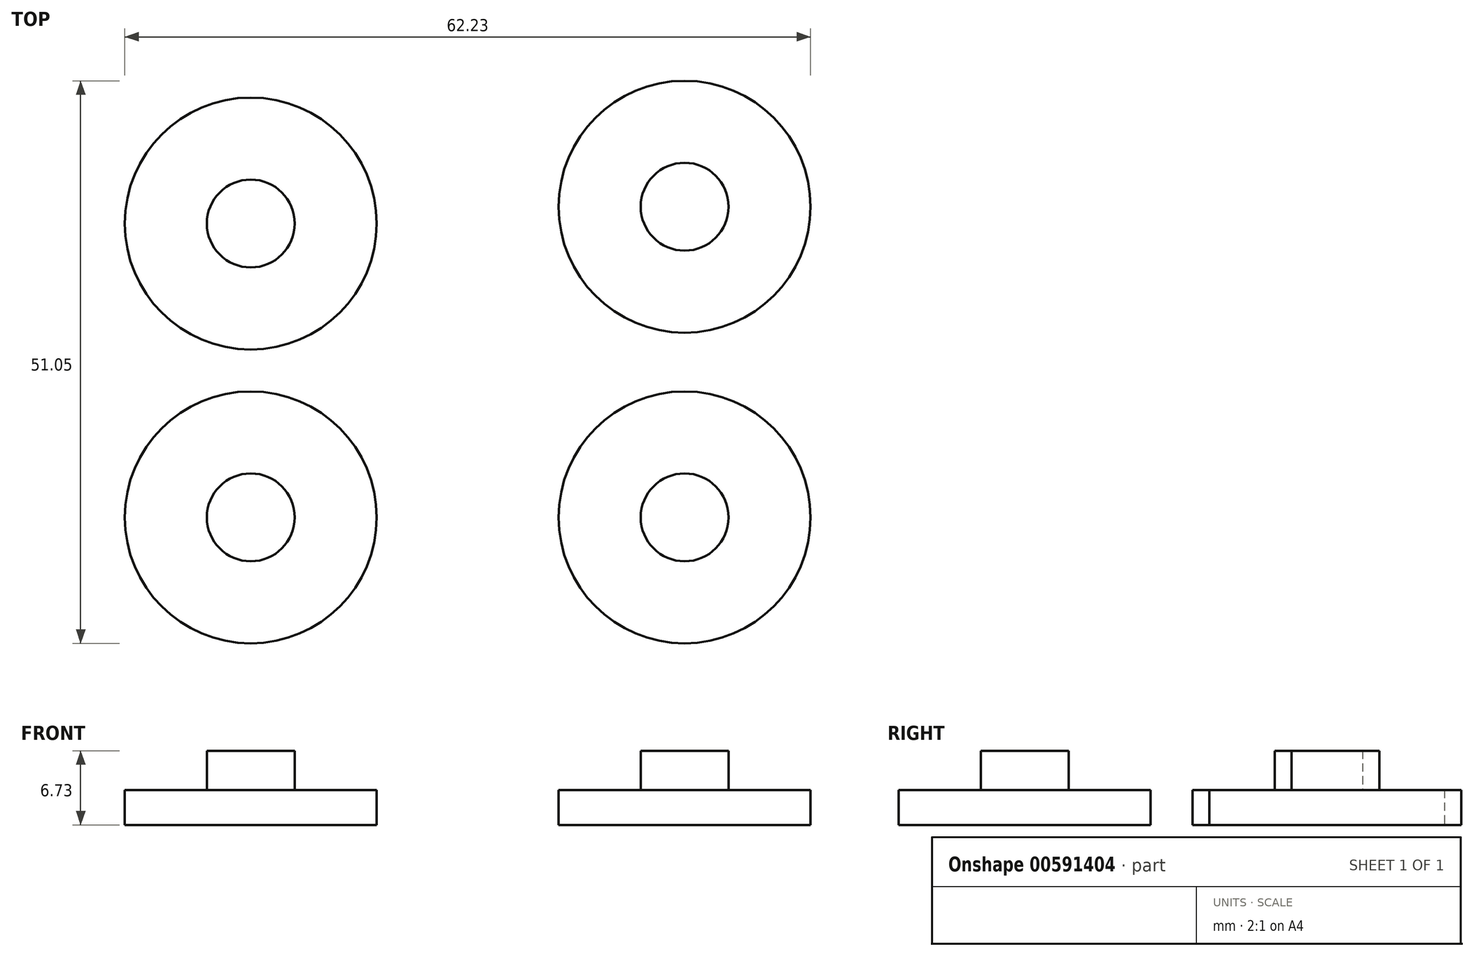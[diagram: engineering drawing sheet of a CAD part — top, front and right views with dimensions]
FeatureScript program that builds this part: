
annotation { "Feature Type Name" : "Feature", "Feature Type Description" : "" }
export const myFeature = defineFeature(function(context is Context, id is Id, definition is map)
    precondition{}
    {
        {
            var Q0;
            Q0=qCreatedBy(makeId("Top.planeOp"),FACE);
            var sketch = newSketch(context, id + "F0", { "sketchPlane" : qUnion([Q0])});
            skCircle(sketch, "E0", {"center": v(0, 0) * mm, "radius": 11.43 * mm});
            skSolve(sketch);
        }
        {
            var Q0;
            Q0=makeQuery(id+"F0.imprint","IMPRINT",FACE,{"disambiguationData":[TD([[makeQuery(id+"F0.imprint","IMPRINT",EDGE,{"derivedFrom":sQuery(id+"F0.wireOp",EDGE,"E0")}),1.0]])]});
            extrude(context, id + "F1", {"entities" : qUnion([Q0]), "depth" : 3.17 * mm, "offsetDistance" : 25.4 * mm});
        }
        {
            var Q0;
            Q0=makeQuery(id+"F1.opExtrude","CAP_FACE",FACE,{"disambiguationData":[OSD([sQuery(id+"F0.wireOp",EDGE,"E0")])],"isStart":false});
            var sketch = newSketch(context, id + "F2", { "sketchPlane" : qUnion([Q0])});
            skCircle(sketch, "E1", {"center": v(0, 0) * mm, "radius": 3.99 * mm});
            skSolve(sketch);
        }
        {
            var Q0;
            Q0=makeQuery(id+"F2.imprint","IMPRINT",FACE,{"disambiguationData":[TD([[makeQuery(id+"F2.imprint","IMPRINT",EDGE,{"derivedFrom":sQuery(id+"F2.wireOp",EDGE,"E1")}),1.0]])]});
            extrude(context, id + "F3", {"entities" : qUnion([Q0]), "operationType" : NewBodyOperationType.ADD, "depth" : 3.56 * mm, "offsetDistance" : 25.4 * mm});
        }
        {
            var Q0;
            Q0=makeQuery(id+"F1.opExtrude","SWEPT_BODY",BODY,{"disambiguationData":[OSD([sQuery(id+"F0.wireOp",EDGE,"E0")])]});
            transform(context, id + "F4", {"entities" : qUnion([Q0]), "transformType" : TransformType.TRANSLATION_3D, "dx" : 39.37 * mm, "dy" : 0 * mm, "dz" : 0 * mm, "makeCopy" : true});
        }
        {
            var Q0;
            Q0=makeQuery(id+"F4.opPattern","COPY",BODY,{"derivedFrom":makeQuery(id+"F1.opExtrude","SWEPT_BODY",BODY,{"disambiguationData":[OSD([sQuery(id+"F0.wireOp",EDGE,"E0")])]}),"instanceName":"1"});
            transform(context, id + "F5", {"entities" : qUnion([Q0]), "transformType" : TransformType.TRANSLATION_3D, "dx" : 0 * mm, "dy" : 28.2 * mm, "dz" : 0 * mm, "makeCopy" : true});
        }
        {
            var Q0;
            Q0=makeQuery(id+"F1.opExtrude","SWEPT_BODY",BODY,{"disambiguationData":[OSD([sQuery(id+"F0.wireOp",EDGE,"E0")])]});
            transform(context, id + "F6", {"entities" : qUnion([Q0]), "transformType" : TransformType.TRANSLATION_3D, "dx" : 0 * mm, "dy" : 26.67 * mm, "dz" : 0 * mm, "makeCopy" : true});
        }
    });
